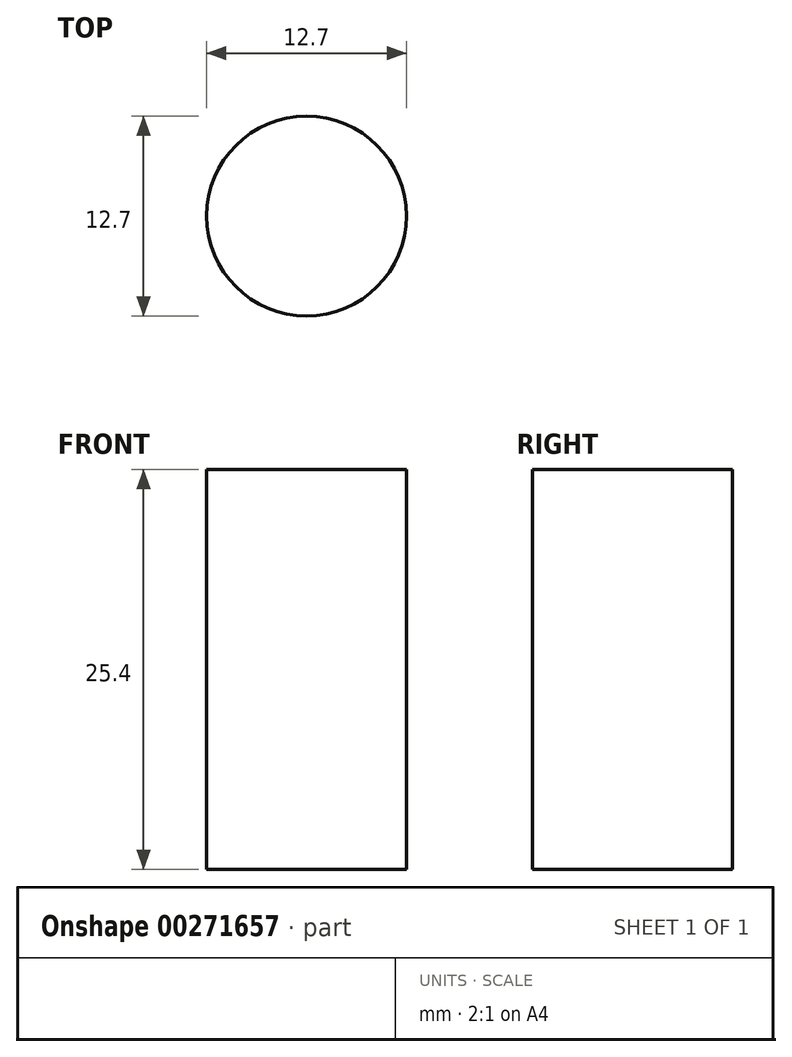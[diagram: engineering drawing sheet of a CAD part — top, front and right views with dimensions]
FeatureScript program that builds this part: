
annotation { "Feature Type Name" : "Feature", "Feature Type Description" : "" }
export const myFeature = defineFeature(function(context is Context, id is Id, definition is map)
    precondition{}
    {
        {
            var Q0;
            Q0=qCreatedBy(makeId("Top.planeOp"),FACE);
            var sketch = newSketch(context, id + "F0", { "sketchPlane" : qUnion([Q0])});
            skCircle(sketch, "E0", {"center": v(0, 0) * mm, "radius": 6.35 * mm});
            skSolve(sketch);
        }
        {
            var Q0;
            Q0=makeQuery(id+"F0.imprint","IMPRINT",FACE,{"disambiguationData":[TD([[makeQuery(id+"F0.imprint","IMPRINT",EDGE,{"derivedFrom":sQuery(id+"F0.wireOp",EDGE,"E0")}),1.0]])]});
            extrude(context, id + "F1", {"entities" : qUnion([Q0]), "oppositeDirection" : true, "depth" : 25.4 * mm});
        }
    });
